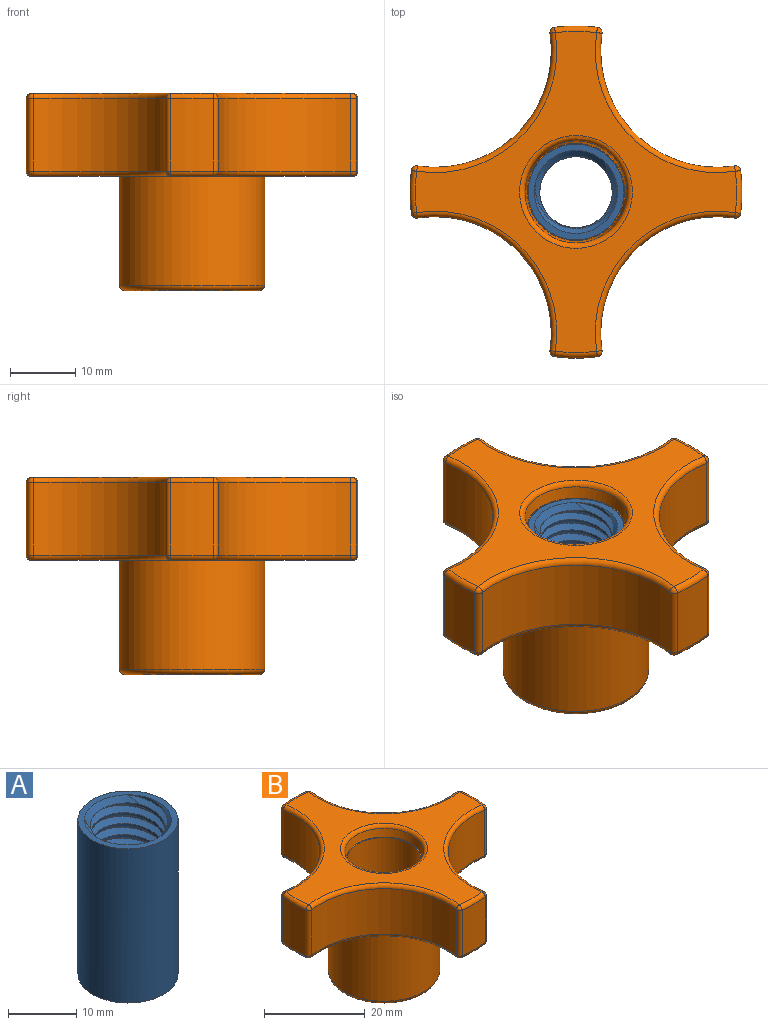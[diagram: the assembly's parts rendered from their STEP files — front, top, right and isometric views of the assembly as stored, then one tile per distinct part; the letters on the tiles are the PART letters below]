
ASSEMBLY  parts=2 mates=1
PART A: 64 faces, bbox 14.7x14.7x28 mm
  f0: cone r=5.43mm half-angle=45deg, axis (0,0,1), area 12mm2, adj f58,f61
  f1: cylinder r=6.35mm len=12.7mm, axis (0,0,-1), area 9.9mm2, adj f2,f59
  f2: cone r=5.54mm half-angle=60deg, axis (0,0.15,-0.99), area 15.1mm2, adj f1,f60,f62
  f3: cone r=6.59mm half-angle=60deg, axis (0,-0.15,0.99), area 31.5mm2, adj f54,f60,f62
  f4: cone r=5.54mm half-angle=60deg, axis (0,0.15,-0.99), area 39.1mm2, adj f5,f54
  f5: cylinder r=5.54mm len=11.07mm, axis (0,-0.15,0.99), area 17mm2, adj f4,f6
  f6: cone r=6.59mm half-angle=60deg, axis (0,-0.15,0.99), area 39.1mm2, adj f5,f53
  f7: cone r=5.54mm half-angle=60deg, axis (0,0.15,-0.99), area 39.1mm2, adj f8,f53
  f8: cylinder r=5.54mm len=11.07mm, axis (0,-0.15,0.99), area 17mm2, adj f7,f9
  f9: cone r=6.59mm half-angle=60deg, axis (0,-0.15,0.99), area 39.1mm2, adj f8,f52
  f10: cone r=5.54mm half-angle=60deg, axis (0,0.15,-0.99), area 39.1mm2, adj f11,f52
  f11: cylinder r=5.54mm len=11.07mm, axis (0,-0.15,0.99), area 17mm2, adj f10,f12
  f12: cone r=6.59mm half-angle=60deg, axis (0,-0.15,0.99), area 39.1mm2, adj f11,f51
  f13: cone r=5.54mm half-angle=60deg, axis (0,0.15,-0.99), area 39.1mm2, adj f14,f51
  f14: cylinder r=5.54mm len=11.07mm, axis (0,-0.15,0.99), area 17mm2, adj f13,f15
  f15: cone r=6.59mm half-angle=60deg, axis (0,-0.15,0.99), area 39.1mm2, adj f14,f50
  f16: cone r=5.54mm half-angle=60deg, axis (0,0.15,-0.99), area 39.1mm2, adj f17,f50
  f17: cylinder r=5.54mm len=11.07mm, axis (0,-0.15,0.99), area 17mm2, adj f16,f18
  f18: cone r=6.59mm half-angle=60deg, axis (0,-0.15,0.99), area 39.1mm2, adj f17,f49
  f19: cone r=5.54mm half-angle=60deg, axis (0,0.15,-0.99), area 39.1mm2, adj f20,f49
  f20: cylinder r=5.54mm len=11.07mm, axis (0,-0.15,0.99), area 17mm2, adj f19,f21
  f21: cone r=6.59mm half-angle=60deg, axis (0,-0.15,0.99), area 39.1mm2, adj f20,f48
  f22: cone r=5.54mm half-angle=60deg, axis (0,0.15,-0.99), area 39.1mm2, adj f23,f48
  f23: cylinder r=5.54mm len=11.07mm, axis (0,-0.15,0.99), area 17mm2, adj f22,f24
  f24: cone r=6.59mm half-angle=60deg, axis (0,-0.15,0.99), area 39.1mm2, adj f23,f47
  f25: cone r=5.54mm half-angle=60deg, axis (0,0.15,-0.99), area 39.1mm2, adj f26,f47
  f26: cylinder r=5.54mm len=11.07mm, axis (0,-0.15,0.99), area 17mm2, adj f25,f27
  f27: cone r=6.59mm half-angle=60deg, axis (0,-0.15,0.99), area 39.1mm2, adj f26,f46
  f28: cone r=5.54mm half-angle=60deg, axis (0,0.15,-0.99), area 39.1mm2, adj f29,f46
  f29: cylinder r=5.54mm len=11.07mm, axis (0,-0.15,0.99), area 17mm2, adj f28,f30
  f30: cone r=6.59mm half-angle=60deg, axis (0,-0.15,0.99), area 39.1mm2, adj f29,f45
  f31: cone r=5.54mm half-angle=60deg, axis (0,0.15,-0.99), area 39.1mm2, adj f32,f45
  f32: cylinder r=5.54mm len=11.07mm, axis (0,-0.15,0.99), area 17mm2, adj f31,f33
  f33: cone r=6.59mm half-angle=60deg, axis (0,-0.15,0.99), area 39.1mm2, adj f32,f44
  f34: cone r=5.54mm half-angle=60deg, axis (0,0.15,-0.99), area 39.1mm2, adj f35,f44
  f35: cylinder r=5.54mm len=11.07mm, axis (0,-0.15,0.99), area 17mm2, adj f34,f36
  f36: cone r=6.59mm half-angle=60deg, axis (0,-0.15,0.99), area 39.1mm2, adj f35,f43
  f37: cone r=5.54mm half-angle=60deg, axis (0,0.15,-0.99), area 39.1mm2, adj f38,f43
  f38: cylinder r=5.54mm len=11.07mm, axis (0,-0.15,0.99), area 17mm2, adj f37,f39
  f39: cone r=6.59mm half-angle=60deg, axis (0,-0.15,0.99), area 39.1mm2, adj f38,f42
  f40: cone r=5.54mm half-angle=60deg, axis (0,0.15,-0.99), area 39.1mm2, adj f41,f42
  f41: cylinder r=5.54mm len=11.07mm, axis (0,-0.15,0.99), area 14.4mm2, adj f40,f55,f63
  f42: cylinder r=6.35mm len=12.7mm, axis (0,0,-1), area 18.3mm2, adj f39,f40
  f43: cylinder r=6.35mm len=12.7mm, axis (0,0,-1), area 18.3mm2, adj f36,f37
  f44: cylinder r=6.35mm len=12.7mm, axis (0,0,-1), area 18.3mm2, adj f33,f34
  f45: cylinder r=6.35mm len=12.7mm, axis (0,0,-1), area 18.3mm2, adj f30,f31
  f46: cylinder r=6.35mm len=12.7mm, axis (0,0,-1), area 18.3mm2, adj f27,f28
  f47: cylinder r=6.35mm len=12.7mm, axis (0,0,-1), area 18.3mm2, adj f24,f25
  f48: cylinder r=6.35mm len=12.7mm, axis (0,0,-1), area 18.3mm2, adj f21,f22
  f49: cylinder r=6.35mm len=12.7mm, axis (0,0,-1), area 18.3mm2, adj f18,f19
  f50: cylinder r=6.35mm len=12.7mm, axis (0,0,-1), area 18.3mm2, adj f15,f16
  f51: cylinder r=6.35mm len=12.7mm, axis (0,0,-1), area 18.3mm2, adj f12,f13
  f52: cylinder r=6.35mm len=12.7mm, axis (0,0,-1), area 18.3mm2, adj f9,f10
  f53: cylinder r=6.35mm len=12.7mm, axis (0,0,-1), area 18.3mm2, adj f6,f7
  f54: cylinder r=6.35mm len=12.7mm, axis (0,0,-1), area 18.3mm2, adj f3,f4
  f55: cone r=6.59mm half-angle=60deg, axis (0,-0.15,0.99), area 26.5mm2, adj f41,f57,f63
  f56: cylinder r=7.33mm len=27.62mm, axis (0,0,-1), area 1271.6mm2, adj f59,f61
  f57: cylinder r=6.35mm len=12.7mm, axis (0,0,-1), area 7.2mm2, adj f55,f58,f61
  f58: cone r=5.54mm half-angle=60deg, axis (0,0.15,-0.99), area 8mm2, adj f0,f57
  f59: plane 14.65x14.65mm, normal (0,0,-1), area 42mm2, adj f1,f56,f62
  f60: cylinder r=5.54mm len=11.07mm, axis (0,-0.15,0.99), area 7.9mm2, adj f2,f3,f62
  f61: plane 14.65x14.65mm, normal (0,0,1), area 42mm2, adj f0,f56,f57,f63
  f62: cone r=6.35mm half-angle=45deg, axis (0,0,-1), area 18.6mm2, adj f2,f3,f59,f60
  f63: cone r=5.43mm half-angle=45deg, axis (0,0,1), area 13mm2, adj f41,f55,f61
PART B: 59 faces, bbox 51.2x51.2x30.2 mm
  f0: cone r=7.35mm half-angle=45deg, axis (0,0,1), area 1.7mm2, adj f21,f36
  f1: cone r=7.35mm half-angle=45deg, axis (0,0,-1), area 1.7mm2, adj f21,f27
  f2: torus R=8.63mm, axis (0,0,-1), area 58.9mm2, adj f14,f24
  f3: torus R=10.29mm, axis (0,0,1), area 88mm2, adj f19,f27
  f4: torus R=24.58mm, axis (0,0,-1), area 8.4mm2, adj f24,f25,f56,f58
  f5: sphere r=0.82mm, area 1.1mm2, adj f6,f29,f53
  f6: torus R=18.6mm, axis (0,0,-1), area 43.9mm2, adj f5,f24,f28,f50
  f7: sphere r=0.82mm, area 1.1mm2, adj f8,f15,f51
  f8: torus R=18.6mm, axis (0,0,-1), area 43.9mm2, adj f7,f24,f31,f48
  f9: torus R=24.58mm, axis (0,0,1), area 8.4mm2, adj f20,f26,f45,f47
  f10: sphere r=0.82mm, area 1.1mm2, adj f29,f43,f46
  f11: sphere r=0.82mm, area 1.1mm2, adj f15,f41,f44
  f12: torus R=18.6mm, axis (0,0,1), area 43.9mm2, adj f18,f26,f39,f42
  f13: torus R=18.6mm, axis (0,0,1), area 43.9mm2, adj f17,f26,f37,f40
  f14: cone r=7.94mm half-angle=10deg, axis (0,0,1), area 90.8mm2, adj f2,f36
  f15: cylinder r=0.82mm len=11.05mm, axis (0,0,1), area 14.5mm2, adj f7,f11,f22,f31
  f16: cylinder r=0.82mm len=11.05mm, axis (0,0,-1), area 14.5mm2, adj f17,f22,f40,f52
  f17: cylinder r=17.78mm len=20.47mm, axis (0,0,1), area 368.4mm2, adj f13,f16,f33,f54
  f18: cylinder r=17.78mm len=20.47mm, axis (0,0,1), area 368.4mm2, adj f12,f30,f32,f57
  f19: cylinder r=11.11mm len=22.23mm, axis (0,0,1), area 1161.7mm2, adj f3,f26
  f20: cylinder r=25.4mm len=11.05mm, axis (0,0,1), area 72.5mm2, adj f9,f34,f35,f49
  f21: cylinder r=7.33mm len=27.57mm, axis (0,0,1), area 1269.3mm2, adj f0,f1
  f22: cylinder r=25.4mm len=11.05mm, axis (0,0,1), area 72.5mm2, adj f15,f16,f41,f51
  f23: cylinder r=25.4mm len=11.05mm, axis (0,0,1), area 72.5mm2, adj f29,f30,f43,f53
  f24: plane 49.15x49.15mm, normal (0,0,1), area 608.3mm2, adj f2,f4,f6,f8,f49,f51,f53,f54
  f25: cylinder r=25.4mm len=11.05mm, axis (0,0,1), area 72.5mm2, adj f4,f32,f33,f38
  f26: plane 49.15x49.15mm, normal (0,0,-1), area 454.3mm2, adj f9,f12,f13,f19,f38,f41,f43,f44
  f27: plane 20.58x20.58mm, normal (0,0,-1), area 162.7mm2, adj f1,f3
  f28: cylinder r=17.78mm len=20.47mm, axis (0,0,1), area 368.4mm2, adj f6,f29,f35,f46
  f29: cylinder r=0.82mm len=11.05mm, axis (0,0,-1), area 14.5mm2, adj f5,f10,f23,f28
  f30: cylinder r=0.82mm len=11.05mm, axis (0,0,1), area 14.5mm2, adj f18,f23,f42,f55
  f31: cylinder r=17.78mm len=20.47mm, axis (0,0,1), area 368.4mm2, adj f8,f15,f34,f44
  f32: cylinder r=0.82mm len=11.05mm, axis (0,0,-1), area 14.5mm2, adj f18,f25,f39,f58
  f33: cylinder r=0.82mm len=11.05mm, axis (0,0,1), area 14.5mm2, adj f17,f25,f37,f56
  f34: cylinder r=0.82mm len=11.05mm, axis (0,0,-1), area 14.5mm2, adj f20,f31,f45,f48
  f35: cylinder r=0.82mm len=11.05mm, axis (0,0,1), area 14.5mm2, adj f20,f28,f47,f50
  f36: plane 14.98x14.98mm, normal (0,0,1), area 6.4mm2, adj f0,f14
  f37: sphere r=0.82mm, area 1.1mm2, adj f13,f33,f38
  f38: torus R=24.58mm, axis (0,0,1), area 8.4mm2, adj f25,f26,f37,f39
  f39: sphere r=0.82mm, area 1.1mm2, adj f12,f32,f38
  f40: sphere r=0.82mm, area 1.1mm2, adj f13,f16,f41
  f41: torus R=24.58mm, axis (0,0,1), area 8.4mm2, adj f11,f22,f26,f40
  f42: sphere r=0.82mm, area 1.1mm2, adj f12,f30,f43
  f43: torus R=24.58mm, axis (0,0,1), area 8.4mm2, adj f10,f23,f26,f42
  f44: torus R=18.6mm, axis (0,0,1), area 43.9mm2, adj f11,f26,f31,f45
  f45: sphere r=0.82mm, area 1.1mm2, adj f9,f34,f44
  f46: torus R=18.6mm, axis (0,0,1), area 43.9mm2, adj f10,f26,f28,f47
  f47: sphere r=0.82mm, area 1.1mm2, adj f9,f35,f46
  f48: sphere r=0.82mm, area 1.1mm2, adj f8,f34,f49
  f49: torus R=24.58mm, axis (0,0,-1), area 8.4mm2, adj f20,f24,f48,f50
  f50: sphere r=0.82mm, area 1.1mm2, adj f6,f35,f49
  f51: torus R=24.58mm, axis (0,0,-1), area 8.4mm2, adj f7,f22,f24,f52
  f52: sphere r=0.82mm, area 1.1mm2, adj f16,f51,f54
  f53: torus R=24.58mm, axis (0,0,-1), area 8.4mm2, adj f5,f23,f24,f55
  f54: torus R=18.6mm, axis (0,0,-1), area 43.9mm2, adj f17,f24,f52,f56
  f55: sphere r=0.82mm, area 1.1mm2, adj f30,f53,f57
  f56: sphere r=0.82mm, area 1.1mm2, adj f4,f33,f54
  f57: torus R=18.6mm, axis (0,0,-1), area 43.9mm2, adj f18,f24,f55,f58
  f58: sphere r=0.82mm, area 1.1mm2, adj f4,f32,f57
PLACE A at identity
PLACE B at identity
MATE fastened A.f1 <-> B.f0  axis (0,0,-1) through (0,0,-15.08)mm
